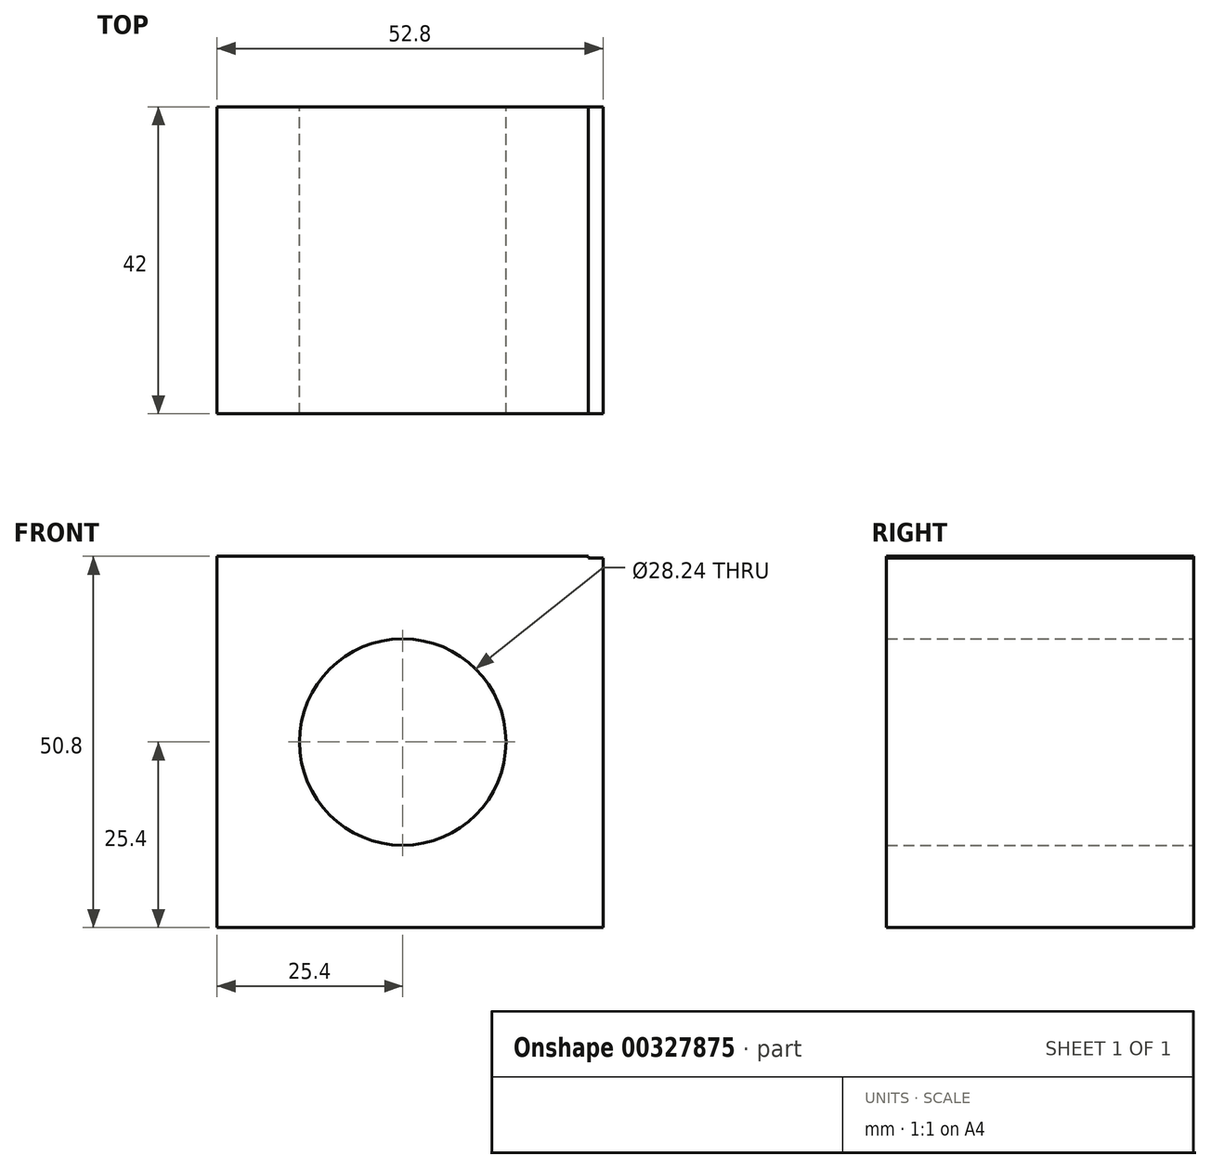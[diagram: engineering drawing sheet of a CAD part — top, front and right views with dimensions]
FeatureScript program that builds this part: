
annotation { "Feature Type Name" : "Feature", "Feature Type Description" : "" }
export const myFeature = defineFeature(function(context is Context, id is Id, definition is map)
    precondition{}
    {
        {
            var Q0;
            Q0=qCreatedBy(makeId("Front.planeOp"),FACE);
            var sketch = newSketch(context, id + "F0", { "sketchPlane" : qUnion([Q0])});
            skLineSegment(sketch, "E0.bottom", {"start": v(-25.4, 25.4) * mm, "end": v(25.4, 25.4) * mm});
            skLineSegment(sketch, "E0.top", {"start": v(-25.4, -25.4) * mm, "end": v(25.4, -25.4) * mm});
            skLineSegment(sketch, "E0.left", {"start": v(-25.4, 25.4) * mm, "end": v(-25.4, -25.4) * mm});
            skLineSegment(sketch, "E0.right", {"start": v(25.4, 25.4) * mm, "end": v(25.4, -25.4) * mm});
            skPoint(sketch, "E0.middle", {"position": v(0, 0) * mm});
            skLineSegment(sketch, "E1.bottom", {"start": v(0, -25.4) * mm, "end": v(0, -25.4) * mm});
            skLineSegment(sketch, "E1.top", {"start": v(0, 76.2) * mm, "end": v(0, 76.2) * mm});
            skLineSegment(sketch, "E1.left", {"start": v(0, -25.4) * mm, "end": v(0, 76.2) * mm, "construction": true});
            skLineSegment(sketch, "E1.right", {"start": v(0, -25.4) * mm, "end": v(0, 76.2) * mm, "construction": true});
            skPoint(sketch, "E1.middle", {"position": v(0, 25.4) * mm});
            skLineSegment(sketch, "E2.bottom", {"start": v(25.4, 0) * mm, "end": v(-76.2, 0) * mm, "construction": true});
            skLineSegment(sketch, "E2.top", {"start": v(25.4, 0) * mm, "end": v(-76.2, 0) * mm, "construction": true});
            skLineSegment(sketch, "E2.left", {"start": v(25.4, 0) * mm, "end": v(25.4, 0) * mm});
            skLineSegment(sketch, "E2.right", {"start": v(-76.2, 0) * mm, "end": v(-76.2, 0) * mm});
            skPoint(sketch, "E2.middle", {"position": v(-25.4, 0) * mm});
            skCircle(sketch, "E3", {"center": v(0, 0) * mm, "radius": 14.12 * mm});
            skLineSegment(sketch, "E4.bottom", {"start": v(25.4, -25.4) * mm, "end": v(27.4, -25.4) * mm});
            skLineSegment(sketch, "E4.top", {"start": v(25.4, 25.17) * mm, "end": v(27.4, 25.17) * mm});
            skLineSegment(sketch, "E4.left", {"start": v(25.4, -25.4) * mm, "end": v(25.4, 25.17) * mm});
            skLineSegment(sketch, "E4.right", {"start": v(27.4, -25.4) * mm, "end": v(27.4, 25.17) * mm});
            skSolve(sketch);
        }
        {
            var Q0;
            Q0=makeQuery(id+"F0.imprint","IMPRINT",FACE,{"disambiguationData":[TD([[makeQuery(id+"F0.imprint","IMPRINT",EDGE,{"derivedFrom":sQuery(id+"F0.wireOp",EDGE,"E0.bottom")}),-1.0]])]});
            extrude(context, id + "F1", {"entities" : qUnion([Q0]), "depth" : 7 * mm});
        }
        {
            var Q0;
            Q0 = qSketchRegion(id + "F0", true);
            extrude(context, id + "F2", {"entities" : qUnion([Q0]), "operationType" : NewBodyOperationType.ADD, "depth" : 42 * mm});
        }
    });
